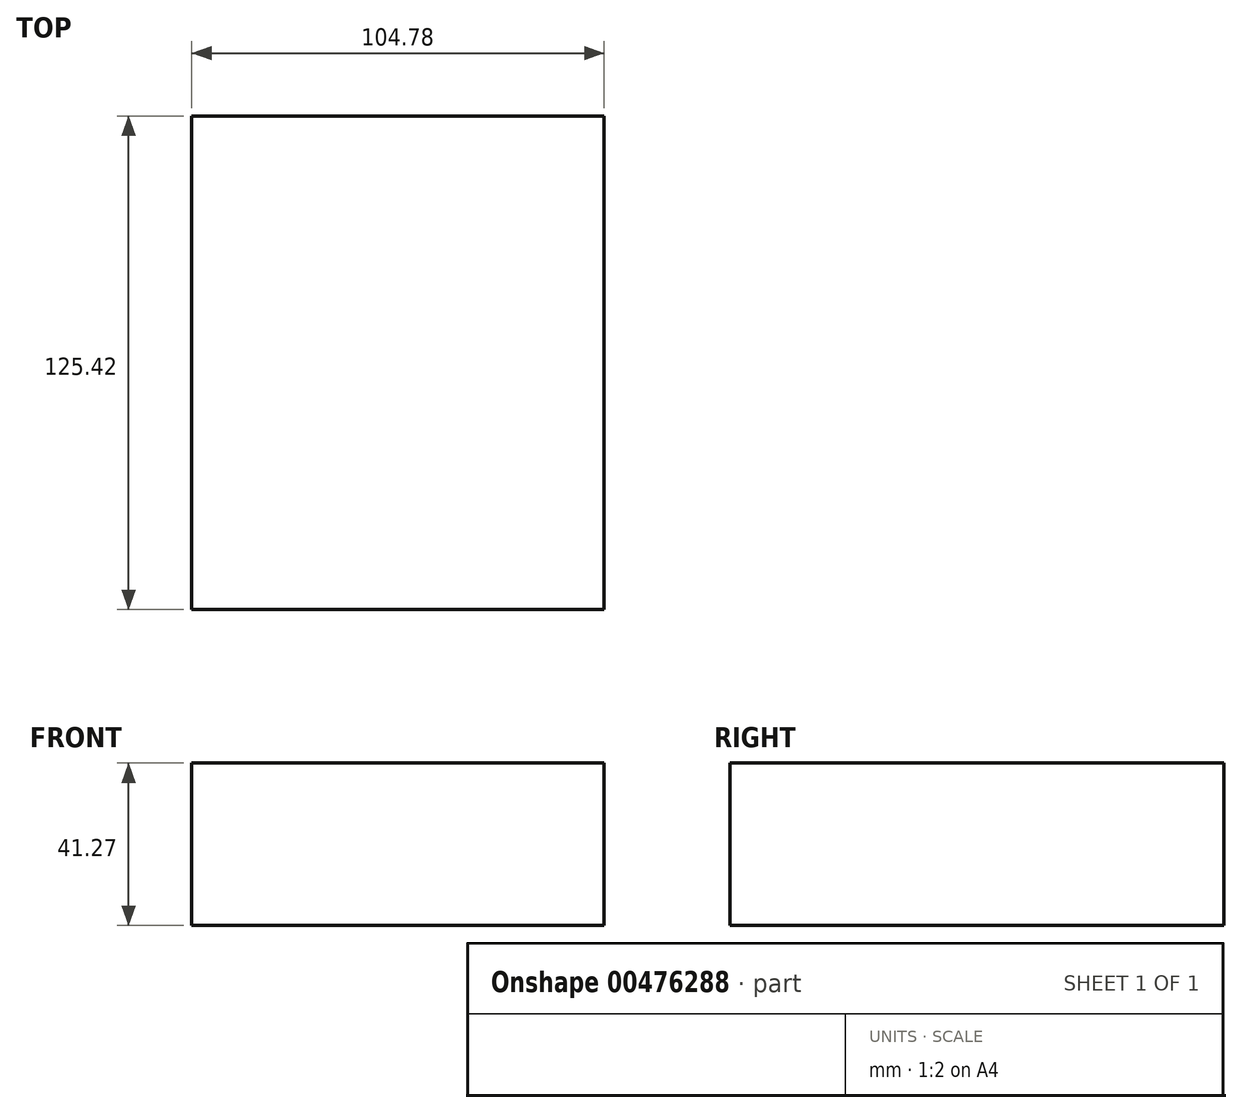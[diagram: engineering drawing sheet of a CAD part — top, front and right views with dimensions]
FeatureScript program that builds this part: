
annotation { "Feature Type Name" : "Feature", "Feature Type Description" : "" }
export const myFeature = defineFeature(function(context is Context, id is Id, definition is map)
    precondition{}
    {
        {
            var Q0;
            Q0=qCreatedBy(makeId("Top.planeOp"),FACE);
            var sketch = newSketch(context, id + "F0", { "sketchPlane" : qUnion([Q0])});
            skLineSegment(sketch, "E0.bottom", {"start": v(-52.39, 62.7) * mm, "end": v(52.39, 62.7) * mm});
            skLineSegment(sketch, "E0.top", {"start": v(-52.39, -62.7) * mm, "end": v(52.39, -62.7) * mm});
            skLineSegment(sketch, "E0.left", {"start": v(-52.39, 62.7) * mm, "end": v(-52.39, -62.7) * mm});
            skLineSegment(sketch, "E0.right", {"start": v(52.39, 62.7) * mm, "end": v(52.39, -62.7) * mm});
            skPoint(sketch, "E0.middle", {"position": v(0, 0) * mm});
            skSolve(sketch);
        }
        {
            var Q0;
            Q0=makeQuery(id+"F0.imprint","IMPRINT",FACE,{"disambiguationData":[TD([[makeQuery(id+"F0.imprint","IMPRINT",EDGE,{"derivedFrom":sQuery(id+"F0.wireOp",EDGE,"E0.bottom")}),-1.0]])]});
            extrude(context, id + "F1", {"entities" : qUnion([Q0]), "depth" : 41.27 * mm});
        }
    });
